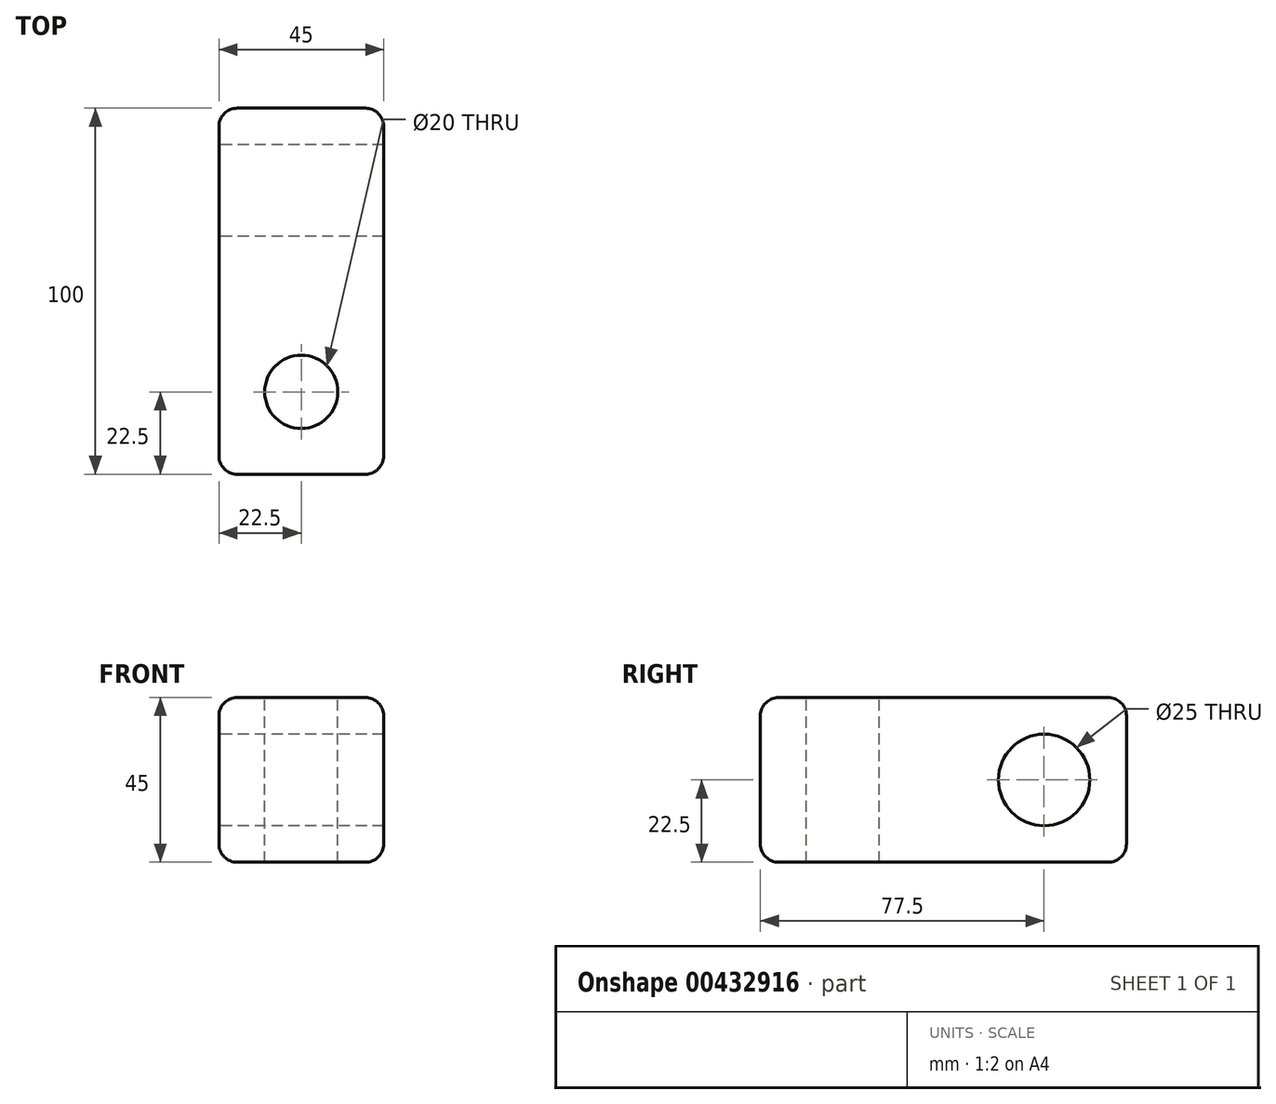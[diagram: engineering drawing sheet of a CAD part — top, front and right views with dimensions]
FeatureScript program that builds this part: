
annotation { "Feature Type Name" : "Feature", "Feature Type Description" : "" }
export const myFeature = defineFeature(function(context is Context, id is Id, definition is map)
    precondition{}
    {
        {
            var Q0;
            Q0=qCreatedBy(makeId("Front.planeOp"),FACE);
            var sketch = newSketch(context, id + "F0", { "sketchPlane" : qUnion([Q0])});
            skLineSegment(sketch, "E0.bottom", {"start": v(0, 0) * mm, "end": v(-45, 0) * mm});
            skLineSegment(sketch, "E0.top", {"start": v(0, 45) * mm, "end": v(-45, 45) * mm});
            skLineSegment(sketch, "E0.left", {"start": v(0, 0) * mm, "end": v(0, 45) * mm});
            skLineSegment(sketch, "E0.right", {"start": v(-45, 0) * mm, "end": v(-45, 45) * mm});
            skSolve(sketch);
        }
        {
            var Q0;
            Q0=qSketchRegion(id+"F0",true);
            extrude(context, id + "F1", {"entities" : qUnion([Q0]), "depth" : 100 * mm});
        }
        {
            var Q0;
            Q0=makeQuery(id+"F1.opExtrude","CAP_FACE",FACE,{"disambiguationData":[OSD([sQuery(id+"F0.wireOp",EDGE,"E0.bottom"),sQuery(id+"F0.wireOp",EDGE,"E0.top"),sQuery(id+"F0.wireOp",EDGE,"E0.left"),sQuery(id+"F0.wireOp",EDGE,"E0.right")])],"isStart":false});
            var Q1;
            Q1=makeQuery(id+"F1.opExtrude","SWEPT_FACE",FACE,{"disambiguationData":[OSD([sQuery(id+"F0.wireOp",EDGE,"E0.right")])]});
            var Q2;
            Q2=makeQuery(id+"F1.opExtrude","SWEPT_FACE",FACE,{"disambiguationData":[OSD([sQuery(id+"F0.wireOp",EDGE,"E0.top")])]});
            var Q3;
            Q3=makeQuery(id+"F1.opExtrude","SWEPT_FACE",FACE,{"disambiguationData":[OSD([sQuery(id+"F0.wireOp",EDGE,"E0.left")])]});
            var Q4;
            Q4=makeQuery(id+"F1.opExtrude","CAP_FACE",FACE,{"disambiguationData":[OSD([sQuery(id+"F0.wireOp",EDGE,"E0.bottom"),sQuery(id+"F0.wireOp",EDGE,"E0.top"),sQuery(id+"F0.wireOp",EDGE,"E0.left"),sQuery(id+"F0.wireOp",EDGE,"E0.right")])],"isStart":true});
            fillet(context, id + "F2", {"entities" : qUnion([Q0, Q1, Q2, Q3, Q4]), "radius" : 5 * mm, "tangentPropagation" : true, "allowEdgeOverflow" : false});
        }
        {
            var Q0;
            Q0=makeQuery(id+"F1.opExtrude","SWEPT_FACE",FACE,{"disambiguationData":[OSD([sQuery(id+"F0.wireOp",EDGE,"E0.top")])]});
            var sketch = newSketch(context, id + "F3", { "sketchPlane" : qUnion([Q0])});
            skCircle(sketch, "E1", {"center": v(-22.5, -77.5) * mm, "radius": 10 * mm});
            skSolve(sketch);
        }
        {
            var Q0;
            Q0=makeQuery(id+"F3.imprint","IMPRINT",FACE,{"disambiguationData":[TD([[makeQuery(id+"F3.imprint","IMPRINT",EDGE,{"derivedFrom":sQuery(id+"F3.wireOp",EDGE,"E1")}),1.0]])]});
            extrude(context, id + "F4", {"entities" : qUnion([Q0]), "operationType" : NewBodyOperationType.REMOVE, "oppositeDirection" : true, "depth" : 45 * mm});
        }
        {
            var Q0;
            Q0=makeQuery(id+"F1.opExtrude","SWEPT_FACE",FACE,{"disambiguationData":[OSD([sQuery(id+"F0.wireOp",EDGE,"E0.right")])]});
            var sketch = newSketch(context, id + "F5", { "sketchPlane" : qUnion([Q0])});
            skCircle(sketch, "E2", {"center": v(22.5, 22.5) * mm, "radius": 12.5 * mm});
            skSolve(sketch);
        }
        {
            var Q0;
            Q0=makeQuery(id+"F5.imprint","IMPRINT",FACE,{"disambiguationData":[TD([[makeQuery(id+"F5.imprint","IMPRINT",EDGE,{"derivedFrom":sQuery(id+"F5.wireOp",EDGE,"E2")}),1.0]])]});
            extrude(context, id + "F6", {"entities" : qUnion([Q0]), "operationType" : NewBodyOperationType.REMOVE, "oppositeDirection" : true, "depth" : 45 * mm});
        }
    });
